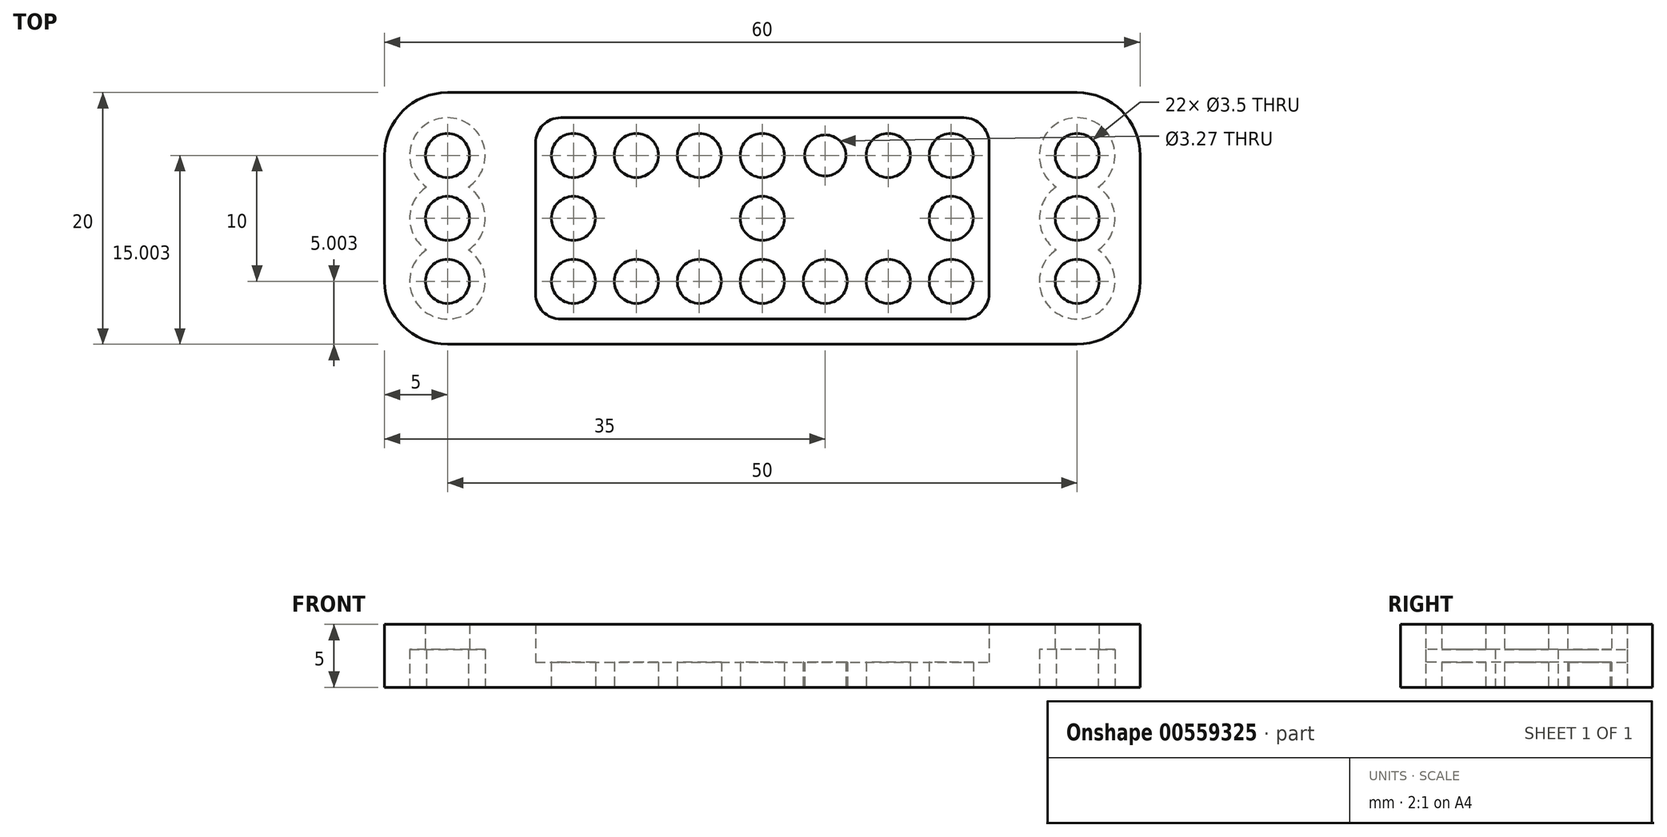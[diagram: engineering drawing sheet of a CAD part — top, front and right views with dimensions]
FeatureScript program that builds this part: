
annotation { "Feature Type Name" : "Feature", "Feature Type Description" : "" }
export const myFeature = defineFeature(function(context is Context, id is Id, definition is map)
    precondition{}
    {
        {
            var Q0;
            Q0=qCreatedBy(makeId("Top.planeOp"),FACE);
            var sketch = newSketch(context, id + "F0", { "sketchPlane" : qUnion([Q0])});
            skLineSegment(sketch, "E0", {"start": v(-31.91, 29.78) * mm, "end": v(18.09, 29.78) * mm, "construction": true});
            skLineSegment(sketch, "E1", {"start": v(-31.91, 29.78) * mm, "end": v(-31.91, 34.78) * mm, "construction": true});
            skLineSegment(sketch, "E2", {"start": v(-31.91, 29.78) * mm, "end": v(-31.91, 24.78) * mm, "construction": true});
            skLineSegment(sketch, "E3", {"start": v(18.09, 29.78) * mm, "end": v(18.09, 24.78) * mm, "construction": true});
            skLineSegment(sketch, "E4", {"start": v(18.09, 29.78) * mm, "end": v(18.09, 34.78) * mm, "construction": true});
            skCircle(sketch, "E5", {"center": v(-31.91, 34.78) * mm, "radius": 1.75 * mm});
            skCircle(sketch, "E6", {"center": v(-31.91, 29.78) * mm, "radius": 1.75 * mm});
            skCircle(sketch, "E7", {"center": v(-31.91, 24.78) * mm, "radius": 1.75 * mm});
            skCircle(sketch, "E8", {"center": v(18.09, 29.78) * mm, "radius": 1.75 * mm});
            skCircle(sketch, "E9", {"center": v(18.09, 34.78) * mm, "radius": 1.75 * mm});
            skCircle(sketch, "E10", {"center": v(18.09, 24.78) * mm, "radius": 1.75 * mm});
            skLineSegment(sketch, "E11", {"start": v(-31.91, 34.78) * mm, "end": v(-31.91, 39.78) * mm, "construction": true});
            skLineSegment(sketch, "E12", {"start": v(-31.91, 34.78) * mm, "end": v(-36.91, 34.78) * mm, "construction": true});
            skLineSegment(sketch, "E13", {"start": v(18.09, 24.78) * mm, "end": v(18.09, 19.78) * mm, "construction": true});
            skLineSegment(sketch, "E14", {"start": v(18.09, 24.78) * mm, "end": v(23.09, 24.78) * mm, "construction": true});
            skLineSegment(sketch, "E15", {"start": v(-36.91, 39.78) * mm, "end": v(23.09, 39.78) * mm});
            skLineSegment(sketch, "E16", {"start": v(23.09, 39.78) * mm, "end": v(23.09, 19.78) * mm});
            skLineSegment(sketch, "E17", {"start": v(23.09, 19.78) * mm, "end": v(-36.91, 19.78) * mm});
            skLineSegment(sketch, "E18", {"start": v(-36.91, 19.78) * mm, "end": v(-36.91, 39.78) * mm});
            skLineSegment(sketch, "E19", {"start": v(-31.91, 34.78) * mm, "end": v(-21.91, 34.78) * mm, "construction": true});
            skLineSegment(sketch, "E20", {"start": v(18.09, 24.78) * mm, "end": v(8.09, 24.78) * mm, "construction": true});
            skCircle(sketch, "E21", {"center": v(-21.91, 34.78) * mm, "radius": 1.75 * mm});
            skCircle(sketch, "E22", {"center": v(8.09, 24.78) * mm, "radius": 1.75 * mm});
            skLineSegment(sketch, "E23", {"start": v(-21.91, 34.78) * mm, "end": v(-16.91, 34.78) * mm, "construction": true});
            skLineSegment(sketch, "E24", {"start": v(-16.91, 34.78) * mm, "end": v(-11.91, 34.78) * mm, "construction": true});
            skLineSegment(sketch, "E25", {"start": v(-11.91, 34.78) * mm, "end": v(-6.91, 34.78) * mm, "construction": true});
            skLineSegment(sketch, "E26", {"start": v(-6.91, 34.78) * mm, "end": v(-1.91, 34.78) * mm, "construction": true});
            skLineSegment(sketch, "E27", {"start": v(-1.91, 34.78) * mm, "end": v(3.09, 34.78) * mm, "construction": true});
            skLineSegment(sketch, "E28", {"start": v(3.09, 34.78) * mm, "end": v(8.09, 34.78) * mm, "construction": true});
            skLineSegment(sketch, "E29", {"start": v(8.09, 24.78) * mm, "end": v(8.09, 34.78) * mm, "construction": true});
            skLineSegment(sketch, "E30", {"start": v(-21.91, 34.78) * mm, "end": v(-21.91, 29.78) * mm, "construction": true});
            skLineSegment(sketch, "E31", {"start": v(-21.91, 29.78) * mm, "end": v(-21.91, 24.78) * mm, "construction": true});
            skLineSegment(sketch, "E32", {"start": v(-21.91, 24.78) * mm, "end": v(8.09, 24.78) * mm, "construction": true});
            skLineSegment(sketch, "E33", {"start": v(-16.91, 34.78) * mm, "end": v(-16.91, 24.78) * mm, "construction": true});
            skLineSegment(sketch, "E34", {"start": v(-11.91, 34.78) * mm, "end": v(-11.91, 24.78) * mm, "construction": true});
            skLineSegment(sketch, "E35", {"start": v(-6.91, 34.78) * mm, "end": v(-6.91, 24.78) * mm, "construction": true});
            skLineSegment(sketch, "E36", {"start": v(3.09, 34.78) * mm, "end": v(3.09, 24.78) * mm, "construction": true});
            skLineSegment(sketch, "E37", {"start": v(-1.91, 34.78) * mm, "end": v(-1.91, 24.78) * mm, "construction": true});
            skCircle(sketch, "E38", {"center": v(-21.91, 24.78) * mm, "radius": 1.75 * mm});
            skCircle(sketch, "E39", {"center": v(-16.91, 24.78) * mm, "radius": 1.75 * mm});
            skCircle(sketch, "E40", {"center": v(-11.91, 24.78) * mm, "radius": 1.75 * mm});
            skCircle(sketch, "E41", {"center": v(-6.91, 24.78) * mm, "radius": 1.75 * mm});
            skCircle(sketch, "E42", {"center": v(-1.91, 24.78) * mm, "radius": 1.75 * mm});
            skCircle(sketch, "E43", {"center": v(3.09, 24.78) * mm, "radius": 1.75 * mm});
            skCircle(sketch, "E44", {"center": v(-6.91, 29.78) * mm, "radius": 1.75 * mm});
            skCircle(sketch, "E45", {"center": v(-6.91, 34.78) * mm, "radius": 1.75 * mm});
            skCircle(sketch, "E46", {"center": v(-1.91, 34.78) * mm, "radius": 1.63 * mm});
            skCircle(sketch, "E47", {"center": v(3.09, 34.78) * mm, "radius": 1.75 * mm});
            skCircle(sketch, "E48", {"center": v(8.09, 34.78) * mm, "radius": 1.75 * mm});
            skCircle(sketch, "E49", {"center": v(8.09, 29.78) * mm, "radius": 1.75 * mm});
            skCircle(sketch, "E50", {"center": v(-21.91, 29.78) * mm, "radius": 1.75 * mm});
            skCircle(sketch, "E51", {"center": v(-16.91, 34.78) * mm, "radius": 1.75 * mm});
            skCircle(sketch, "E52", {"center": v(-11.91, 34.78) * mm, "radius": 1.75 * mm});
            skLineSegment(sketch, "E53", {"start": v(8.09, 34.78) * mm, "end": v(11.09, 34.78) * mm, "construction": true});
            skLineSegment(sketch, "E54", {"start": v(8.09, 34.78) * mm, "end": v(8.09, 37.78) * mm, "construction": true});
            skLineSegment(sketch, "E55", {"start": v(-21.91, 24.78) * mm, "end": v(-24.91, 24.78) * mm, "construction": true});
            skLineSegment(sketch, "E56", {"start": v(11.09, 37.78) * mm, "end": v(-24.91, 37.78) * mm});
            skLineSegment(sketch, "E57", {"start": v(-21.91, 24.78) * mm, "end": v(-21.91, 21.78) * mm, "construction": true});
            skLineSegment(sketch, "E58", {"start": v(-24.91, 37.78) * mm, "end": v(-24.91, 21.78) * mm});
            skLineSegment(sketch, "E59", {"start": v(-24.91, 21.78) * mm, "end": v(11.09, 21.78) * mm});
            skLineSegment(sketch, "E60", {"start": v(11.09, 21.78) * mm, "end": v(11.09, 37.78) * mm});
            skArc(sketch, "E61", {"start": v(-33.57, 27.28) * mm, "mid": v(-31.91, 21.78) * mm, "end": v(-30.25, 27.28) * mm});
            skLineSegment(sketch, "E62", {"start": v(-33.57, 27.28) * mm, "end": v(-33.57, 27.28) * mm});
            skArc(sketch, "E63", {"start": v(-30.25, 27.28) * mm, "mid": v(-28.91, 29.78) * mm, "end": v(-30.25, 32.28) * mm});
            skArc(sketch, "E64", {"start": v(-33.57, 32.28) * mm, "mid": v(-34.91, 29.78) * mm, "end": v(-33.57, 27.28) * mm});
            skArc(sketch, "E65", {"start": v(-30.25, 32.28) * mm, "mid": v(-31.91, 37.78) * mm, "end": v(-33.57, 32.28) * mm});
            skLineSegment(sketch, "E66", {"start": v(-30.25, 27.28) * mm, "end": v(-30.25, 27.28) * mm});
            skArc(sketch, "E67", {"start": v(16.43, 27.28) * mm, "mid": v(18.09, 21.78) * mm, "end": v(19.75, 27.28) * mm});
            skArc(sketch, "E68", {"start": v(19.75, 32.28) * mm, "mid": v(18.09, 37.78) * mm, "end": v(16.43, 32.28) * mm});
            skArc(sketch, "E69", {"start": v(16.43, 32.28) * mm, "mid": v(15.09, 29.78) * mm, "end": v(16.43, 27.28) * mm});
            skLineSegment(sketch, "E70", {"start": v(16.43, 27.28) * mm, "end": v(16.43, 27.28) * mm});
            skArc(sketch, "E71", {"start": v(19.75, 27.28) * mm, "mid": v(21.09, 29.78) * mm, "end": v(19.75, 32.28) * mm});
            skSolve(sketch);
        }
        {
            var Q0;
            Q0=makeQuery(id+"F0.imprint","IMPRINT",FACE,{"disambiguationData":[TD([[makeQuery(id+"F0.imprint","IMPRINT",EDGE,{"derivedFrom":sQuery(id+"F0.wireOp",EDGE,"E21")}),-1.0]])]});
            extrude(context, id + "F1", {"entities" : qUnion([Q0]), "depth" : 2 * mm, "offsetDistance" : 25 * mm});
        }
        {
            var Q0;
            Q0=makeQuery(id+"F0.imprint","IMPRINT",FACE,{"disambiguationData":[TD([[makeQuery(id+"F0.imprint","IMPRINT",EDGE,{"derivedFrom":sQuery(id+"F0.wireOp",EDGE,"E15")}),-1.0]])]});
            extrude(context, id + "F2", {"entities" : qUnion([Q0]), "operationType" : NewBodyOperationType.ADD, "depth" : 3 * mm, "offsetDistance" : 25 * mm});
        }
        {
            var Q0;
            Q0=makeQuery(id+"F2.opExtrude","CAP_FACE",FACE,{"disambiguationData":[OSD([sQuery(id+"F0.wireOp",EDGE,"E15"),sQuery(id+"F0.wireOp",EDGE,"E16"),sQuery(id+"F0.wireOp",EDGE,"E17"),sQuery(id+"F0.wireOp",EDGE,"E18"),sQuery(id+"F0.wireOp",EDGE,"E56"),sQuery(id+"F0.wireOp",EDGE,"E58"),sQuery(id+"F0.wireOp",EDGE,"E59"),sQuery(id+"F0.wireOp",EDGE,"E60"),sQuery(id+"F0.wireOp",EDGE,"E61"),sQuery(id+"F0.wireOp",EDGE,"E63"),sQuery(id+"F0.wireOp",EDGE,"E64"),sQuery(id+"F0.wireOp",EDGE,"E65"),sQuery(id+"F0.wireOp",EDGE,"E67"),sQuery(id+"F0.wireOp",EDGE,"E68"),sQuery(id+"F0.wireOp",EDGE,"E69"),sQuery(id+"F0.wireOp",EDGE,"E71")])],"isStart":false});
            var sketch = newSketch(context, id + "F3", { "sketchPlane" : qUnion([Q0])});
            skLineSegment(sketch, "E72", {"start": v(-36.91, 39.78) * mm, "end": v(23.09, 39.78) * mm});
            skLineSegment(sketch, "E73", {"start": v(23.09, 39.78) * mm, "end": v(23.09, 19.78) * mm});
            skLineSegment(sketch, "E74", {"start": v(-36.91, 19.78) * mm, "end": v(-36.91, 39.78) * mm});
            skLineSegment(sketch, "E75", {"start": v(-36.91, 19.78) * mm, "end": v(23.09, 19.78) * mm});
            skSolve(sketch);
        }
        {
            var Q0;
            Q0=makeQuery(id+"F3.imprint","IMPRINT",FACE,{"disambiguationData":[TD([[makeQuery(id+"F3.imprint","IMPRINT",EDGE,{"derivedFrom":sQuery(id+"F3.wireOp",EDGE,"E72")}),-1.0]])]});
            var Q1;
            Q1=makeQuery(id+"F3.imprint","IMPRINT",FACE,{"disambiguationData":[TD([[makeQuery(id+"F3.imprint","IMPRINT",EDGE,{"derivedFrom":makeQuery(id+"F2.opExtrude","CAP_EDGE",EDGE,{"disambiguationData":[OSD([sQuery(id+"F0.wireOp",EDGE,"E67")])],"isStart":false})}),1.0]])]});
            var Q2;
            Q2=makeQuery(id+"F3.imprint","IMPRINT",FACE,{"disambiguationData":[TD([[makeQuery(id+"F3.imprint","IMPRINT",EDGE,{"derivedFrom":makeQuery(id+"F2.opExtrude","CAP_EDGE",EDGE,{"disambiguationData":[OSD([sQuery(id+"F0.wireOp",EDGE,"E61")])],"isStart":false})}),1.0]])]});
            extrude(context, id + "F4", {"entities" : qUnion([Q0, Q1, Q2]), "operationType" : NewBodyOperationType.ADD, "depth" : 2 * mm, "offsetDistance" : 25 * mm});
        }
        {
            var Q0;
            Q0=makeQuery(id+"F0.imprint","IMPRINT",FACE,{"disambiguationData":[TD([[makeQuery(id+"F0.imprint","IMPRINT",EDGE,{"derivedFrom":sQuery(id+"F0.wireOp",EDGE,"E5")}),1.0]])]});
            var Q1;
            Q1=makeQuery(id+"F0.imprint","IMPRINT",FACE,{"disambiguationData":[TD([[makeQuery(id+"F0.imprint","IMPRINT",EDGE,{"derivedFrom":sQuery(id+"F0.wireOp",EDGE,"E6")}),1.0]])]});
            var Q2;
            Q2=makeQuery(id+"F0.imprint","IMPRINT",FACE,{"disambiguationData":[TD([[makeQuery(id+"F0.imprint","IMPRINT",EDGE,{"derivedFrom":sQuery(id+"F0.wireOp",EDGE,"E7")}),1.0]])]});
            var Q3;
            Q3=makeQuery(id+"F0.imprint","IMPRINT",FACE,{"disambiguationData":[TD([[makeQuery(id+"F0.imprint","IMPRINT",EDGE,{"derivedFrom":sQuery(id+"F0.wireOp",EDGE,"E10")}),1.0]])]});
            var Q4;
            Q4=makeQuery(id+"F0.imprint","IMPRINT",FACE,{"disambiguationData":[TD([[makeQuery(id+"F0.imprint","IMPRINT",EDGE,{"derivedFrom":sQuery(id+"F0.wireOp",EDGE,"E9")}),1.0]])]});
            var Q5;
            Q5=makeQuery(id+"F0.imprint","IMPRINT",FACE,{"disambiguationData":[TD([[makeQuery(id+"F0.imprint","IMPRINT",EDGE,{"derivedFrom":sQuery(id+"F0.wireOp",EDGE,"E8")}),1.0]])]});
            extrude(context, id + "F5", {"entities" : qUnion([Q0, Q1, Q2, Q3, Q4, Q5]), "operationType" : NewBodyOperationType.REMOVE, "depth" : 25 * mm, "offsetDistance" : 25 * mm});
        }
        {
            var Q0;
            Q0=makeQuery(id+"F4.boolean.opBoolean","MERGE",EDGE,{"derivedFrom":[makeQuery(id+"F2.opExtrude","SWEPT_EDGE",EDGE,{"disambiguationData":[OSD([sQuery(id+"F0.wireOp",EDGE,"E15"),sQuery(id+"F0.wireOp",EDGE,"E18")])]}),makeQuery(id+"F4.opExtrude","SWEPT_EDGE",EDGE,{"disambiguationData":[OSD([sQuery(id+"F3.wireOp",EDGE,"E72"),sQuery(id+"F3.wireOp",EDGE,"E74")])]})]});
            var Q1;
            Q1=makeQuery(id+"F4.boolean.opBoolean","MERGE",EDGE,{"derivedFrom":[makeQuery(id+"F2.opExtrude","SWEPT_EDGE",EDGE,{"disambiguationData":[OSD([sQuery(id+"F0.wireOp",EDGE,"E17"),sQuery(id+"F0.wireOp",EDGE,"E18")])]}),makeQuery(id+"F4.opExtrude","SWEPT_EDGE",EDGE,{"disambiguationData":[OSD([sQuery(id+"F3.wireOp",EDGE,"E74"),sQuery(id+"F3.wireOp",EDGE,"E75")])]})]});
            var Q2;
            Q2=makeQuery(id+"F4.boolean.opBoolean","MERGE",EDGE,{"derivedFrom":[makeQuery(id+"F2.opExtrude","SWEPT_EDGE",EDGE,{"disambiguationData":[OSD([sQuery(id+"F0.wireOp",EDGE,"E16"),sQuery(id+"F0.wireOp",EDGE,"E17")])]}),makeQuery(id+"F4.opExtrude","SWEPT_EDGE",EDGE,{"disambiguationData":[OSD([sQuery(id+"F3.wireOp",EDGE,"E73"),sQuery(id+"F3.wireOp",EDGE,"E75")])]})]});
            var Q3;
            Q3=makeQuery(id+"F4.boolean.opBoolean","MERGE",EDGE,{"derivedFrom":[makeQuery(id+"F2.opExtrude","SWEPT_EDGE",EDGE,{"disambiguationData":[OSD([sQuery(id+"F0.wireOp",EDGE,"E15"),sQuery(id+"F0.wireOp",EDGE,"E16")])]}),makeQuery(id+"F4.opExtrude","SWEPT_EDGE",EDGE,{"disambiguationData":[OSD([sQuery(id+"F3.wireOp",EDGE,"E72"),sQuery(id+"F3.wireOp",EDGE,"E73")])]})]});
            fillet(context, id + "F6", {"entities" : qUnion([Q0, Q1, Q2, Q3]), "radius" : 5 * mm, "tangentPropagation" : true, "allowEdgeOverflow" : false});
        }
        {
            var Q0;
            {var subQ0=sQuery(id+"F0.wireOp",EDGE,"E58");var subQ1=sQuery(id+"F0.wireOp",EDGE,"E56");Q0=makeQuery(id+"F4.boolean.opBoolean","MERGE",EDGE,{"derivedFrom":[makeQuery(id+"F2.opExtrude","SWEPT_EDGE",EDGE,{"disambiguationData":[OSD([subQ1,subQ0])]}),makeQuery(id+"F4.opExtrude","SWEPT_EDGE",EDGE,{"disambiguationData":[OSD([subQ1,subQ0])]})]});}
            var Q1;
            {var subQ0=sQuery(id+"F0.wireOp",EDGE,"E60");var subQ1=sQuery(id+"F0.wireOp",EDGE,"E59");Q1=makeQuery(id+"F4.boolean.opBoolean","MERGE",EDGE,{"derivedFrom":[makeQuery(id+"F2.opExtrude","SWEPT_EDGE",EDGE,{"disambiguationData":[OSD([subQ1,subQ0])]}),makeQuery(id+"F4.opExtrude","SWEPT_EDGE",EDGE,{"disambiguationData":[OSD([subQ1,subQ0])]})]});}
            var Q2;
            {var subQ0=sQuery(id+"F0.wireOp",EDGE,"E60");var subQ1=sQuery(id+"F0.wireOp",EDGE,"E56");Q2=makeQuery(id+"F4.boolean.opBoolean","MERGE",EDGE,{"derivedFrom":[makeQuery(id+"F2.opExtrude","SWEPT_EDGE",EDGE,{"disambiguationData":[OSD([subQ1,subQ0])]}),makeQuery(id+"F4.opExtrude","SWEPT_EDGE",EDGE,{"disambiguationData":[OSD([subQ1,subQ0])]})]});}
            var Q3;
            {var subQ0=sQuery(id+"F0.wireOp",EDGE,"E59");var subQ1=sQuery(id+"F0.wireOp",EDGE,"E58");Q3=makeQuery(id+"F4.boolean.opBoolean","MERGE",EDGE,{"derivedFrom":[makeQuery(id+"F2.opExtrude","SWEPT_EDGE",EDGE,{"disambiguationData":[OSD([subQ1,subQ0])]}),makeQuery(id+"F4.opExtrude","SWEPT_EDGE",EDGE,{"disambiguationData":[OSD([subQ1,subQ0])]})]});}
            fillet(context, id + "F7", {"entities" : qUnion([Q0, Q1, Q2, Q3]), "radius" : 2 * mm, "tangentPropagation" : true, "allowEdgeOverflow" : false});
        }
    });
